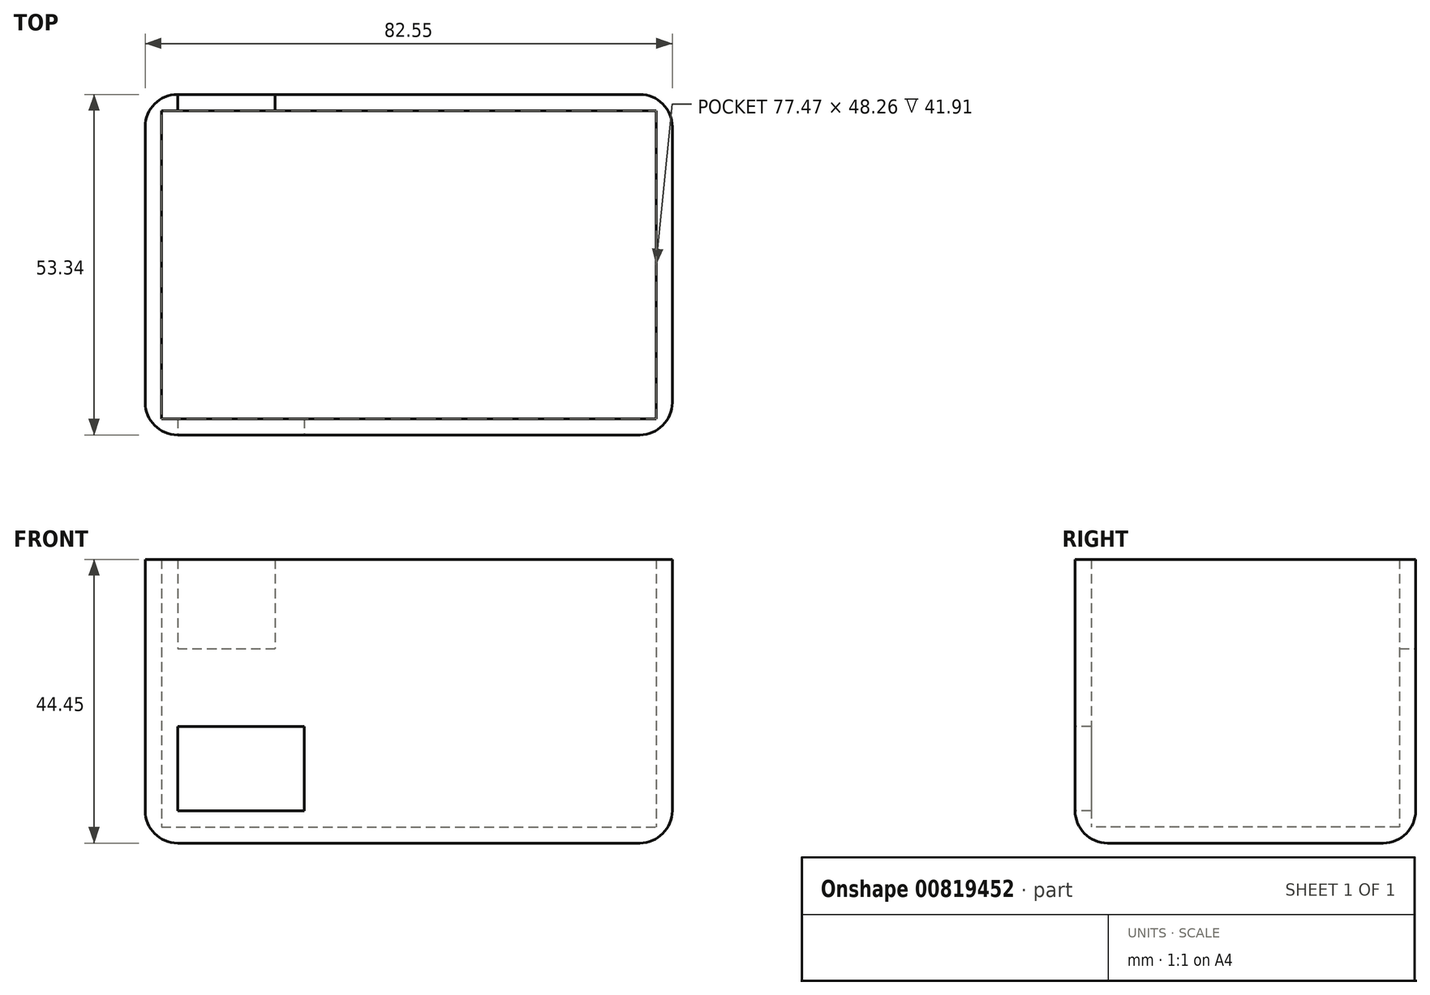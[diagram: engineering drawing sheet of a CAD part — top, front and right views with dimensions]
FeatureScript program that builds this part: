
annotation { "Feature Type Name" : "Feature", "Feature Type Description" : "" }
export const myFeature = defineFeature(function(context is Context, id is Id, definition is map)
    precondition{}
    {
        {
            var Q0;
            Q0=qCreatedBy(makeId("Top.planeOp"),FACE);
            var sketch = newSketch(context, id + "F0", { "sketchPlane" : qUnion([Q0])});
            skLineSegment(sketch, "E0", {"start": v(-38.1, 1.2) * mm, "end": v(-38.1, 27.86) * mm});
            skLineSegment(sketch, "E1", {"start": v(-38.1, 1.2) * mm, "end": v(-38.1, -25.48) * mm});
            skLineSegment(sketch, "E2", {"start": v(44.45, 1.2) * mm, "end": v(44.45, 27.86) * mm});
            skLineSegment(sketch, "E3", {"start": v(44.45, 1.2) * mm, "end": v(44.45, -25.48) * mm});
            skLineSegment(sketch, "E4", {"start": v(-38.1, -25.48) * mm, "end": v(44.45, -25.48) * mm});
            skLineSegment(sketch, "E5", {"start": v(-38.1, 27.86) * mm, "end": v(44.45, 27.86) * mm});
            skSolve(sketch);
        }
        {
            var Q0;
            Q0 = qSketchRegion(id + "F0", true);
            extrude(context, id + "F1", {"entities" : qUnion([Q0]), "depth" : 44.45 * mm, "offsetDistance" : 25.4 * mm});
        }
        {
            var Q0;
            Q0=makeQuery(id+"F1.opExtrude","CAP_FACE",FACE,{"disambiguationData":[OSD([sQuery(id+"F0.wireOp",EDGE,"E0"),sQuery(id+"F0.wireOp",EDGE,"E1"),sQuery(id+"F0.wireOp",EDGE,"E2"),sQuery(id+"F0.wireOp",EDGE,"E3"),sQuery(id+"F0.wireOp",EDGE,"E4"),sQuery(id+"F0.wireOp",EDGE,"E5")])],"isStart":false});
            shell(context, id + "F2", {"entities" : qUnion([Q0]), "thickness" : 2.54 * mm});
        }
        {
            var Q0;
            Q0=makeQuery(id+"F1.opExtrude","SWEPT_EDGE",EDGE,{"disambiguationData":[OSD([sQuery(id+"F0.wireOp",EDGE,"E0"),sQuery(id+"F0.wireOp",EDGE,"E5")])]});
            var Q1;
            Q1=makeQuery(id+"F1.opExtrude","SWEPT_EDGE",EDGE,{"disambiguationData":[OSD([sQuery(id+"F0.wireOp",EDGE,"E1"),sQuery(id+"F0.wireOp",EDGE,"E4")])]});
            var Q2;
            Q2=makeQuery(id+"F1.opExtrude","SWEPT_EDGE",EDGE,{"disambiguationData":[OSD([sQuery(id+"F0.wireOp",EDGE,"E3"),sQuery(id+"F0.wireOp",EDGE,"E4")])]});
            var Q3;
            Q3=makeQuery(id+"F1.opExtrude","SWEPT_EDGE",EDGE,{"disambiguationData":[OSD([sQuery(id+"F0.wireOp",EDGE,"E2"),sQuery(id+"F0.wireOp",EDGE,"E5")])]});
            fillet(context, id + "F3", {"entities" : qUnion([Q0, Q1, Q2, Q3]), "radius" : 5.08 * mm, "tangentPropagation" : true, "allowEdgeOverflow" : false});
        }
        {
            var Q0;
            Q0=makeQuery(id+"F1.opExtrude","CAP_FACE",FACE,{"disambiguationData":[OSD([sQuery(id+"F0.wireOp",EDGE,"E0"),sQuery(id+"F0.wireOp",EDGE,"E1"),sQuery(id+"F0.wireOp",EDGE,"E2"),sQuery(id+"F0.wireOp",EDGE,"E3"),sQuery(id+"F0.wireOp",EDGE,"E4"),sQuery(id+"F0.wireOp",EDGE,"E5")])],"isStart":true});
            fillet(context, id + "F4", {"entities" : qUnion([Q0]), "radius" : 5.08 * mm, "tangentPropagation" : true, "allowEdgeOverflow" : false});
        }
        {
            var Q0;
            Q0=makeQuery(id+"F1.opExtrude","SWEPT_FACE",FACE,{"disambiguationData":[OSD([sQuery(id+"F0.wireOp",EDGE,"E4")])]});
            var sketch = newSketch(context, id + "F5", { "sketchPlane" : qUnion([Q0])});
            skLineSegment(sketch, "E6.bottom", {"start": v(-33.02, 5.08) * mm, "end": v(-13.2, 5.08) * mm});
            skLineSegment(sketch, "E6.top", {"start": v(-33.02, 18.29) * mm, "end": v(-13.2, 18.29) * mm});
            skLineSegment(sketch, "E6.left", {"start": v(-33.02, 5.08) * mm, "end": v(-33.02, 18.29) * mm});
            skLineSegment(sketch, "E6.right", {"start": v(-13.2, 5.08) * mm, "end": v(-13.2, 18.29) * mm});
            skSolve(sketch);
        }
        {
            var Q0;
            Q0 = qSketchRegion(id + "F5", true);
            extrude(context, id + "F6", {"entities" : qUnion([Q0]), "operationType" : NewBodyOperationType.REMOVE, "oppositeDirection" : true, "depth" : 5.6 * mm, "offsetDistance" : 25.4 * mm});
        }
        {
            var Q0;
            Q0=makeQuery(id+"F1.opExtrude","SWEPT_FACE",FACE,{"disambiguationData":[OSD([sQuery(id+"F0.wireOp",EDGE,"E5")])]});
            var sketch = newSketch(context, id + "F7", { "sketchPlane" : qUnion([Q0])});
            skLineSegment(sketch, "E7", {"start": v(33.02, 5.08) * mm, "end": v(33.02, 30.48) * mm, "construction": true});
            skLineSegment(sketch, "E8.bottom", {"start": v(33.02, 30.48) * mm, "end": v(17.78, 30.48) * mm});
            skLineSegment(sketch, "E8.top", {"start": v(33.02, 45.8) * mm, "end": v(17.78, 45.8) * mm});
            skLineSegment(sketch, "E8.left", {"start": v(33.02, 45.8) * mm, "end": v(33.02, 30.48) * mm});
            skLineSegment(sketch, "E8.right", {"start": v(17.78, 45.8) * mm, "end": v(17.78, 30.48) * mm});
            skSolve(sketch);
        }
        {
            var Q0;
            Q0 = qSketchRegion(id + "F7", true);
            extrude(context, id + "F8", {"entities" : qUnion([Q0]), "operationType" : NewBodyOperationType.REMOVE, "oppositeDirection" : true, "depth" : 6.6 * mm, "offsetDistance" : 25.4 * mm});
        }
    });
